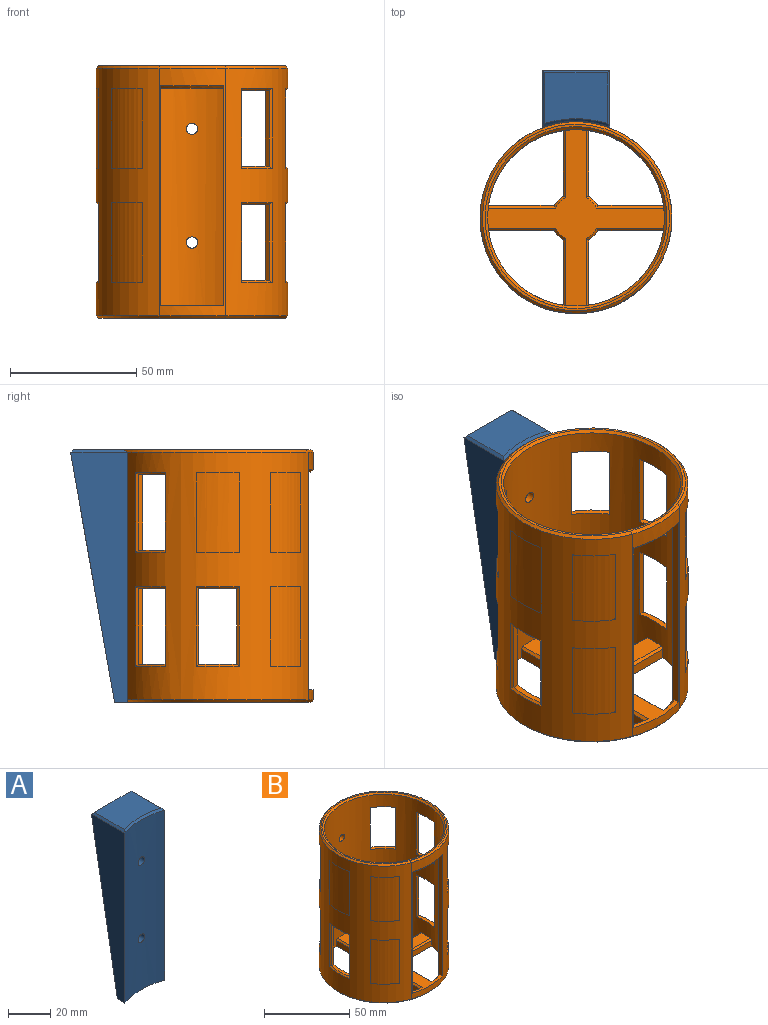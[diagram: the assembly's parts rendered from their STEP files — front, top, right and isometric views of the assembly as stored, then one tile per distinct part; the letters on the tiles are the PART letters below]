
ASSEMBLY  parts=2 mates=1
PART A: 12 faces, bbox 27.4x22.4x100 mm
  f0: cylinder r=40.5mm len=99mm, axis (0,0,-1), area 2669mm2, adj f2,f3,f5,f6,f7,f11
  f1: plane 98.83x26.77mm, normal (0,0.98,-0.17), area 2653.9mm2, adj f2,f3,f5,f6,f7,f8
  f2: plane 99x22.43mm, normal (-1,0,0), area 1359.1mm2, adj f0,f1,f5,f8,f9
  f3: plane 99x22.43mm, normal (1,0,0), area 1359.1mm2, adj f0,f1,f5,f8,f10
  f4: plane 24.77x20.06mm, normal (0,0,1), area 465.4mm2, adj f8,f9,f10,f11
  f5: plane 26.77x5mm, normal (0,0,-1), area 93mm2, adj f0,f1,f2,f3
  f6: cylinder r=2.25mm len=16.41mm, axis (0,-1,0), area 225.9mm2, adj f0,f1
  f7: cylinder r=2.25mm len=8.48mm, axis (0,-1,0), area 113.7mm2, adj f0,f1
  f8: plane 26.77x1.17mm, normal (0,0.77,0.64), area 39.7mm2, adj f1,f2,f3,f4,f9,f10
  f9: plane 22.3x1.02mm, normal (-0.71,0,0.71), area 29.9mm2, adj f2,f4,f8,f11
  f10: plane 22.3x1.02mm, normal (0.71,0,0.71), area 29.9mm2, adj f3,f4,f8,f11
  f11: cone r=41.5mm half-angle=45deg, axis (0,0,1), area 37.1mm2, adj f0,f4,f9,f10
PART B: 148 faces, bbox 76x75.8x100 mm
  f0: plane 25.98x4mm, normal (0,1,0), area 103.9mm2, adj f1,f2,f3,f4
  f1: cylinder r=10mm len=4mm, axis (0,0,-1), area 20.9mm2, adj f0,f4,f5,f6
  f2: plane 26.73x1.03mm, normal (0,0.71,0.71), area 37.3mm2, adj f0,f3,f6,f7
  f3: cylinder r=35mm len=99mm, axis (0,0,-1), area 13862.6mm2, adj f0,f2,f4,f5,f7,f8,f9,f10
  f4: plane 74x73.82mm, normal (0,0,-1), area 1775.9mm2, adj f0,f1,f3,f5,f17,f18,f24,f25
  f5: plane 25.98x4mm, normal (1,0,0), area 103.9mm2, adj f1,f3,f4,f27
  f6: cone r=9mm half-angle=45deg, axis (0,0,-1), area 7.9mm2, adj f1,f2,f7,f27
  f7: plane 72.82x70mm, normal (0,0,1), area 1149.4mm2, adj f2,f3,f6,f16,f19,f20,f22,f23
  f8: cone r=35mm half-angle=45deg, axis (0,0,1), area 38.2mm2, adj f3,f9,f89
  f9: cone r=35mm half-angle=45deg, axis (0,0,1), area 277.2mm2, adj f3,f8,f89
  f10: plane 15.35x2.99mm, normal (0,0,-1), area 33mm2, adj f3,f11,f33,f90,f91,f92
  f11: plane 30x2.05mm, normal (0,1,0), area 61.6mm2, adj f3,f10,f12,f90
  f12: plane 15.35x2.99mm, normal (0,0,1), area 33mm2, adj f3,f11,f33,f90,f92,f93
  f13: plane 15.35x2.99mm, normal (0,0,-1), area 33mm2, adj f3,f14,f32,f94,f95,f96
  f14: plane 30x2.05mm, normal (0,1,0), area 61.6mm2, adj f3,f13,f15,f94
  f15: plane 15.35x2.99mm, normal (0,0,1), area 33mm2, adj f3,f14,f32,f94,f96,f97
  f16: plane 26.73x1.03mm, normal (0,-0.71,0.71), area 37.3mm2, adj f3,f7,f17,f86
  f17: plane 25.98x4mm, normal (0,-1,0), area 103.9mm2, adj f3,f4,f16,f78
  f18: plane 25.98x4mm, normal (-1,0,0), area 103.9mm2, adj f3,f4,f78,f87
  f19: cone r=35mm half-angle=45deg, axis (0,0,1), area 11.6mm2, adj f3,f7,f20,f87
  f20: plane 88.13x3.18mm, normal (1,0,0), area 275mm2, adj f3,f7,f19,f21,f88,f98,f99
  f21: cone r=36mm half-angle=45deg, axis (0,0,-1), area 36mm2, adj f3,f20,f22,f98
  f22: plane 88.13x3.17mm, normal (-1,0,0), area 274.4mm2, adj f3,f7,f21,f23,f88,f98,f99
  f23: cone r=35mm half-angle=45deg, axis (0,0,1), area 11.7mm2, adj f3,f7,f22,f83
  f24: plane 25.98x4mm, normal (1,0,0), area 103.9mm2, adj f3,f4,f76,f83
  f25: plane 25.98x4mm, normal (0,-1,0), area 103.9mm2, adj f3,f4,f26,f76
  f26: plane 26.73x1.03mm, normal (0,-0.71,0.71), area 37.3mm2, adj f3,f7,f25,f84
  f27: plane 26.73x1.03mm, normal (0.71,0,0.71), area 37.3mm2, adj f3,f5,f6,f7
  f28: plane 26.73x1.03mm, normal (-0.71,0,0.71), area 37.3mm2, adj f3,f7,f29,f85
  f29: plane 25.98x4mm, normal (-1,0,0), area 103.9mm2, adj f3,f4,f28,f77
  f30: plane 25.98x4mm, normal (0,1,0), area 103.9mm2, adj f3,f4,f31,f77
  f31: plane 26.73x1.03mm, normal (0,0.71,0.71), area 37.3mm2, adj f3,f7,f30,f85
  f32: plane 30x2.05mm, normal (0,-1,0), area 61.6mm2, adj f3,f13,f15,f96
  f33: plane 30x2.05mm, normal (0,-1,0), area 61.6mm2, adj f3,f10,f12,f92
  f34: cylinder r=2.25mm len=4.5mm, axis (0,-1,0), area 42.5mm2, adj f3,f100
  f35: plane 12.46x12.1mm, normal (0,0,1), area 33mm2, adj f3,f36,f38,f101,f102,f103
  f36: plane 30x1.48mm, normal (0.72,0.69,0), area 61.6mm2, adj f3,f35,f37,f101
  f37: plane 12.46x12.1mm, normal (0,0,-1), area 33mm2, adj f3,f36,f38,f101,f103,f104
  f38: plane 30x1.48mm, normal (-0.72,-0.69,0), area 61.6mm2, adj f3,f35,f37,f103
  f39: plane 12.46x12.1mm, normal (0,0,1), area 33mm2, adj f3,f40,f42,f105,f106,f107
  f40: plane 30x1.48mm, normal (-0.72,-0.69,0), area 61.6mm2, adj f3,f39,f41,f105
  f41: plane 12.46x12.1mm, normal (0,0,-1), area 33mm2, adj f3,f40,f42,f105,f107,f108
  f42: plane 30x1.48mm, normal (0.72,0.69,0), area 61.6mm2, adj f3,f39,f41,f107
  f43: plane 30x2.05mm, normal (0,-1,0), area 61.6mm2, adj f3,f44,f46,f109
  f44: plane 15.35x2.99mm, normal (0,0,1), area 33mm2, adj f3,f43,f45,f109,f110,f111
  f45: plane 30x2.05mm, normal (0,1,0), area 61.6mm2, adj f3,f44,f46,f110
  f46: plane 15.35x2.99mm, normal (0,0,-1), area 33mm2, adj f3,f43,f45,f109,f110,f112
  f47: plane 30x2.05mm, normal (0,-1,0), area 61.6mm2, adj f3,f48,f50,f113
  f48: plane 15.35x2.99mm, normal (0,0,1), area 33mm2, adj f3,f47,f49,f113,f114,f115
  f49: plane 30x2.05mm, normal (0,1,0), area 61.6mm2, adj f3,f48,f50,f114
  f50: plane 15.35x2.99mm, normal (0,0,-1), area 33mm2, adj f3,f47,f49,f113,f114,f116
  f51: plane 30x1.48mm, normal (-0.72,-0.69,0), area 61.6mm2, adj f3,f52,f54,f117
  f52: plane 12.46x12.1mm, normal (0,0,-1), area 33mm2, adj f3,f51,f53,f117,f118,f119
  f53: plane 30x1.48mm, normal (0.72,0.69,0), area 61.6mm2, adj f3,f52,f54,f118
  f54: plane 12.46x12.1mm, normal (0,0,1), area 33mm2, adj f3,f51,f53,f117,f118,f120
  f55: plane 30x1.48mm, normal (0.72,0.69,0), area 61.6mm2, adj f3,f56,f58,f121
  f56: plane 12.46x12.1mm, normal (0,0,-1), area 33mm2, adj f3,f55,f57,f121,f122,f123
  f57: plane 30x1.48mm, normal (-0.72,-0.69,0), area 61.6mm2, adj f3,f56,f58,f122
  f58: plane 12.46x12.1mm, normal (0,0,1), area 33mm2, adj f3,f55,f57,f121,f122,f124
  f59: plane 30x1.48mm, normal (-0.72,0.69,0), area 61.6mm2, adj f3,f60,f62,f125
  f60: plane 12.46x12.1mm, normal (0,0,1), area 33mm2, adj f3,f59,f61,f125,f126,f127
  f61: plane 30x1.48mm, normal (0.72,-0.69,0), area 61.6mm2, adj f3,f60,f62,f126
  f62: plane 12.46x12.1mm, normal (0,0,-1), area 33mm2, adj f3,f59,f61,f125,f126,f128
  f63: plane 30x1.48mm, normal (0.72,-0.69,0), area 61.6mm2, adj f3,f64,f66,f129
  f64: plane 12.46x12.1mm, normal (0,0,1), area 33mm2, adj f3,f63,f65,f129,f130,f131
  f65: plane 30x1.48mm, normal (-0.72,0.69,0), area 61.6mm2, adj f3,f64,f66,f130
  f66: plane 12.46x12.1mm, normal (0,0,-1), area 33mm2, adj f3,f63,f65,f129,f130,f132
  f67: plane 30x1.48mm, normal (-0.72,0.69,0), area 61.6mm2, adj f3,f68,f70,f133
  f68: plane 12.46x12.1mm, normal (0,0,1), area 33mm2, adj f3,f67,f69,f133,f134,f135
  f69: plane 30x1.48mm, normal (0.72,-0.69,0), area 61.6mm2, adj f3,f68,f70,f134
  f70: plane 12.46x12.1mm, normal (0,0,-1), area 33mm2, adj f3,f67,f69,f133,f134,f136
  f71: plane 30x1.48mm, normal (0.72,-0.69,0), area 61.6mm2, adj f3,f72,f74,f137
  f72: plane 12.46x12.1mm, normal (0,0,1), area 33mm2, adj f3,f71,f73,f137,f138,f139
  f73: plane 30x1.48mm, normal (-0.72,0.69,0), area 61.6mm2, adj f3,f72,f74,f138
  f74: plane 12.46x12.1mm, normal (0,0,-1), area 33mm2, adj f3,f71,f73,f137,f138,f140
  f75: cylinder r=2.25mm len=4.5mm, axis (0,-1,0), area 42.5mm2, adj f3,f100
  f76: cylinder r=10mm len=4mm, axis (0,0,-1), area 20.9mm2, adj f4,f24,f25,f84
  f77: cylinder r=10mm len=4mm, axis (0,0,-1), area 20.9mm2, adj f4,f29,f30,f85
  f78: cylinder r=10mm len=4mm, axis (0,0,-1), area 20.9mm2, adj f4,f17,f18,f86
  f79: plane 1.08x1.01mm, normal (1,0,0), area 0mm2, adj f4,f80,f82
  f80: cone r=41mm half-angle=45deg, axis (0,0,1), area 38mm2, adj f4,f79,f81,f88
  f81: plane 1.07x1.01mm, normal (-1,0,0), area 0mm2, adj f4,f80,f82
  f82: cone r=38mm half-angle=45deg, axis (0,0,1), area 295.1mm2, adj f4,f79,f81,f100
  f83: plane 27.74x1.03mm, normal (0.71,0,0.71), area 38mm2, adj f7,f23,f24,f84
  f84: cone r=9mm half-angle=45deg, axis (0,0,-1), area 7.9mm2, adj f7,f26,f76,f83
  f85: cone r=9mm half-angle=45deg, axis (0,0,-1), area 7.9mm2, adj f7,f28,f31,f77
  f86: cone r=9mm half-angle=45deg, axis (0,0,-1), area 7.9mm2, adj f7,f16,f78,f87
  f87: plane 27.74x1.03mm, normal (-0.71,0,0.71), area 38mm2, adj f7,f18,f19,f86
  f88: cylinder r=41mm len=98mm, axis (0,0,-1), area 425.7mm2, adj f7,f20,f22,f80,f99,f100,f141
  f89: plane 74x73.82mm, normal (0,0,1), area 226.1mm2, adj f8,f9,f141,f142,f143,f144
  f90: plane 31.65x1.01mm, normal (-0.78,0.62,0), area 39.3mm2, adj f10,f11,f12,f91,f93,f145
  f91: cone r=37.18mm half-angle=45deg, axis (0,0,1), area 18.9mm2, adj f10,f90,f92,f145
  f92: plane 31.65x1.01mm, normal (-0.78,-0.62,0), area 39.3mm2, adj f10,f12,f33,f91,f93,f145
  f93: cone r=38mm half-angle=45deg, axis (0,0,-1), area 18.9mm2, adj f12,f90,f92,f145
  f94: plane 31.65x1.01mm, normal (-0.78,0.62,0), area 39.3mm2, adj f13,f14,f15,f95,f97,f100
  f95: cone r=37.18mm half-angle=45deg, axis (0,0,1), area 18.9mm2, adj f13,f94,f96,f100
  f96: plane 31.65x1.01mm, normal (-0.78,-0.62,0), area 39.3mm2, adj f13,f15,f32,f95,f97,f100
  f97: cone r=38mm half-angle=45deg, axis (0,0,-1), area 18.9mm2, adj f15,f94,f96,f100
  f98: plane 24.94x3.05mm, normal (0,0,-1), area 22.3mm2, adj f20,f21,f22,f99
  f99: cone r=41mm half-angle=45deg, axis (0,0,1), area 35.9mm2, adj f20,f22,f88,f98
  f100: cylinder r=38mm len=98mm, axis (0,0,-1), area 15842.3mm2, adj f34,f75,f82,f88,f94,f95,f96,f97
  f101: plane 31.65x1.28mm, normal (0.99,-0.13,0), area 39.3mm2, adj f35,f36,f37,f100,f102,f104
  f102: cone r=38mm half-angle=45deg, axis (0,0,-1), area 18.9mm2, adj f35,f100,f101,f103
  f103: plane 31.65x1.28mm, normal (0.09,-1,0), area 39.3mm2, adj f35,f37,f38,f100,f102,f104
  f104: cone r=38mm half-angle=45deg, axis (0,0,1), area 18.9mm2, adj f37,f100,f101,f103
  f105: plane 31.65x1.28mm, normal (-0.99,0.13,0), area 39.3mm2, adj f39,f40,f41,f100,f106,f108
  f106: cone r=38mm half-angle=45deg, axis (0,0,-1), area 18.9mm2, adj f39,f100,f105,f107
  f107: plane 31.65x1.28mm, normal (-0.09,1,0), area 39.3mm2, adj f39,f41,f42,f100,f106,f108
  f108: cone r=38mm half-angle=45deg, axis (0,0,1), area 18.9mm2, adj f41,f100,f105,f107
  f109: plane 31.65x1.01mm, normal (0.78,-0.62,0), area 39.3mm2, adj f43,f44,f46,f100,f111,f112
  f110: plane 31.65x1.01mm, normal (0.78,0.62,0), area 39.3mm2, adj f44,f45,f46,f100,f111,f112
  f111: cone r=38mm half-angle=45deg, axis (0,0,-1), area 18.9mm2, adj f44,f100,f109,f110
  f112: cone r=37.18mm half-angle=45deg, axis (0,0,1), area 18.9mm2, adj f46,f100,f109,f110
  f113: plane 31.65x1.01mm, normal (0.78,-0.62,0), area 39.3mm2, adj f47,f48,f50,f100,f115,f116
  f114: plane 31.65x1.01mm, normal (0.78,0.62,0), area 39.3mm2, adj f48,f49,f50,f100,f115,f116
  f115: cone r=38mm half-angle=45deg, axis (0,0,-1), area 18.9mm2, adj f48,f100,f113,f114
  f116: cone r=37.18mm half-angle=45deg, axis (0,0,1), area 18.9mm2, adj f50,f100,f113,f114
  f117: plane 31.65x1.28mm, normal (-0.99,0.13,0), area 39.3mm2, adj f51,f52,f54,f100,f119,f120
  f118: plane 31.65x1.28mm, normal (-0.09,1,0), area 39.3mm2, adj f52,f53,f54,f100,f119,f120
  f119: cone r=38mm half-angle=45deg, axis (0,0,1), area 18.9mm2, adj f52,f100,f117,f118
  f120: cone r=37.18mm half-angle=45deg, axis (0,0,-1), area 18.9mm2, adj f54,f100,f117,f118
  f121: plane 31.65x1.28mm, normal (0.99,-0.13,0), area 39.3mm2, adj f55,f56,f58,f100,f123,f124
  f122: plane 31.65x1.28mm, normal (0.09,-1,0), area 39.3mm2, adj f56,f57,f58,f100,f123,f124
  f123: cone r=38mm half-angle=45deg, axis (0,0,1), area 18.9mm2, adj f56,f100,f121,f122
  f124: cone r=37.18mm half-angle=45deg, axis (0,0,-1), area 18.9mm2, adj f58,f100,f121,f122
  f125: plane 31.65x1.28mm, normal (-0.99,-0.13,0), area 39.3mm2, adj f59,f60,f62,f127,f128,f146
  f126: plane 31.65x1.28mm, normal (-0.09,-1,0), area 39.3mm2, adj f60,f61,f62,f127,f128,f146
  f127: cone r=38mm half-angle=45deg, axis (0,0,-1), area 18.9mm2, adj f60,f125,f126,f146
  f128: cone r=37.18mm half-angle=45deg, axis (0,0,1), area 18.9mm2, adj f62,f125,f126,f146
  f129: plane 31.65x1.28mm, normal (0.99,0.13,0), area 39.3mm2, adj f63,f64,f66,f100,f131,f132
  f130: plane 31.65x1.28mm, normal (0.09,1,0), area 39.3mm2, adj f64,f65,f66,f100,f131,f132
  f131: cone r=38mm half-angle=45deg, axis (0,0,-1), area 18.9mm2, adj f64,f100,f129,f130
  f132: cone r=37.18mm half-angle=45deg, axis (0,0,1), area 18.9mm2, adj f66,f100,f129,f130
  f133: plane 31.65x1.28mm, normal (-0.99,-0.13,0), area 39.3mm2, adj f67,f68,f70,f135,f136,f147
  f134: plane 31.65x1.28mm, normal (-0.09,-1,0), area 39.3mm2, adj f68,f69,f70,f135,f136,f147
  f135: cone r=38mm half-angle=45deg, axis (0,0,-1), area 18.9mm2, adj f68,f133,f134,f147
  f136: cone r=37.18mm half-angle=45deg, axis (0,0,1), area 18.9mm2, adj f70,f133,f134,f147
  f137: plane 31.65x1.28mm, normal (0.99,0.13,0), area 39.3mm2, adj f71,f72,f74,f100,f139,f140
  f138: plane 31.65x1.28mm, normal (0.09,1,0), area 39.3mm2, adj f72,f73,f74,f100,f139,f140
  f139: cone r=38mm half-angle=45deg, axis (0,0,-1), area 18.9mm2, adj f72,f100,f137,f138
  f140: cone r=37.18mm half-angle=45deg, axis (0,0,1), area 18.9mm2, adj f74,f100,f137,f138
  f141: cone r=40mm half-angle=45deg, axis (0,0,-1), area 38mm2, adj f88,f89,f142,f143
  f142: plane 1.07x1.01mm, normal (-1,0,0), area 0mm2, adj f89,f141,f144
  f143: plane 1.08x1.01mm, normal (1,0,0), area 0mm2, adj f89,f141,f144
  f144: cone r=37mm half-angle=45deg, axis (0,0,-1), area 295.1mm2, adj f89,f100,f142,f143
  f145: cylinder r=38mm len=31.64mm, axis (0,0,-1), area 542.6mm2, adj f90,f91,f92,f93
  f146: cylinder r=38mm len=31.64mm, axis (0,0,-1), area 542.6mm2, adj f125,f126,f127,f128
  f147: cylinder r=38mm len=31.64mm, axis (0,0,-1), area 542.6mm2, adj f133,f134,f135,f136
PLACE A t=(0,-19.37,0)mm
PLACE B at identity
MATE fastened A.f6 <-> B.f34  axis (0,-1,0) through (0,38.02,75)mm
